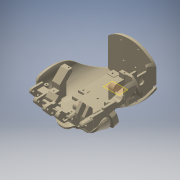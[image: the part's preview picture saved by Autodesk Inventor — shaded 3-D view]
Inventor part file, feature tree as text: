
AUTODESK INVENTOR PART (.ipt)
format: ipt  version: 2018 (Build 220112000, 112)  size: 6,155,264 bytes
history: native  units: mm
features: other x96, reference x14, sketch x11, extrude x11, fillet x2, projected_geometry x1
ambient origin geometry x8: Origin, YZ Plane, XZ Plane, XY Plane, X Axis, Y Axis, Z Axis, Center Point
bodies: Body1 (feature_tree)
feature tree (135):
  other  "ソリッド1"
  other  "ダイレクト編集1"
  other  "ダイレクト編集2"
  other  "ダイレクト編集3"
  other  "ダイレクト編集4"
  other  "ダイレクト編集5"
  other  "ダイレクト編集7"
  other  "ダイレクト編集8"
  other  "ダイレクト編集9"
  sketch  "スケッチ1"
  other  "作業平面1"
  extrude  "押し出し1"  Depth=8.8365mm
  other  "ダイレクト編集10"
  sketch  "スケッチ2"
  other  "作業平面2"
  extrude  "押し出し2"  Depth=7.0mm
  extrude  "押し出し3"  TaperAngle=0.0deg  [1 undecoded]
  extrude  "押し出し4"  Depth=5.0mm
  other  "ダイレクト編集11"
  other  "ダイレクト編集12"
  other  "ダイレクト編集13"
  extrude  "押し出し5"  Depth=2.2mm
  extrude  "押し出し6"  Depth=2.2mm
  other  "ダイレクト編集14"
  other  "ダイレクト編集15"
  fillet  "フィレット1"  Radius=2.2mm
  other  "ダイレクト編集16"
  other  "作業平面3"
  extrude  "押し出し7"  Depth=2.2mm
  extrude  "押し出し8"  Depth=2.2mm
  extrude  "押し出し9"  Depth=2.2mm
  other  "ダイレクト編集17"
  other  "ダイレクト編集18"
  other  "ダイレクト編集19"
  other  "ダイレクト編集20"
  other  "ダイレクト編集21"
  extrude  "押し出し10"  Depth=2.2mm
  other  "ダイレクト編集22"
  other  "ダイレクト編集23"
  extrude  "押し出し11"  Depth=2.2mm
  fillet  "フィレット2"  Radius=2.2mm
  sketch  "スケッチ3"
  reference  "参照1"
  sketch  "スケッチ4"
  reference  "参照2"
  sketch  "スケッチ5"
  reference  "参照3"
  reference  "参照4"
  reference  "参照5"
  reference  "参照6"
  reference  "参照7"
  reference  "参照8"
  sketch  "スケッチ6"
  reference  "参照9"
  reference  "参照10"
  sketch  "スケッチ7"
  reference  "参照11"
  sketch  "スケッチ8"
  sketch  "スケッチ9"
  reference  "参照12"
  sketch  "スケッチ10"
  projected_geometry  "投影ループ1"
  sketch  "スケッチ11"
  reference  "参照13"
  reference  "参照14"
  other  "尺度1"
  other  "サイズ1"
  other  "移動1"
  other  "サイズ2"
  other  "サイズ3"
  other  "サイズ4"
  other  "サイズ5"
  other  "サイズ6"
  other  "サイズ7"
  other  "サイズ8"
  other  "サイズ9"
  other  "サイズ10"
  other  "サイズ11"
  other  "サイズ12"
  other  "サイズ13"
  other  "サイズ14"
  other  "サイズ15"
  other  "削除1"
  other  "削除2"
  other  "削除5"
  other  "削除6"
  other  "削除7"
  other  "移動2"
  other  "移動3"
  other  "移動4"
  other  "移動5"
  parser-record x2  (decoder bookkeeping rows leaked as tree rows — omitted from the tree; the rows remain in map.json)
  other  "M-R-H.iam"
  other  "GWS_Micro2BBMG:1"
  other  "削除8"
  other  "削除9"
  other  "削除10"
  other  "削除11"
  other  "削除12"
  other  "削除13"
  other  "削除14"
  other  "削除15"
  other  "削除16"
  other  "削除17"
  other  "移動6"
  other  "ASV-15MG:1"
  other  "MotorHolder_forM:1"
  other  "移動7"
  other  "移動8"
  other  "移動9"
  other  "削除18"
  other  "サイズ16"
  other  "移動10"
  other  "MJ179PH:1"
  other  "サイズ17"
  other  "サイズ18"
  other  "移動11"
  other  "サイズ19"
  other  "サイズ20"
  other  "サイズ21"
  other  "サイズ22"
  other  "サイズ23"
  other  "サイズ24"
  other  "サイズ25"
  other  "サイズ26"
  other  "削除19"
  other  "移動12"
  other  "移動13"
  other  "移動14"
  other  "移動15"
  other  "移動16"
  other  "移動17"
  other  "移動18"
  other  "Pololu_A_Star_32U4_Micro:1"
note: 1 required parameter value undecoded (feature->parameter linkage not recoverable at this tier; creation-order binding heuristic only, values carry confidence <= 0.55)
note: 2 file-system paths scrubbed to <path> (originals preserved in map.json)
